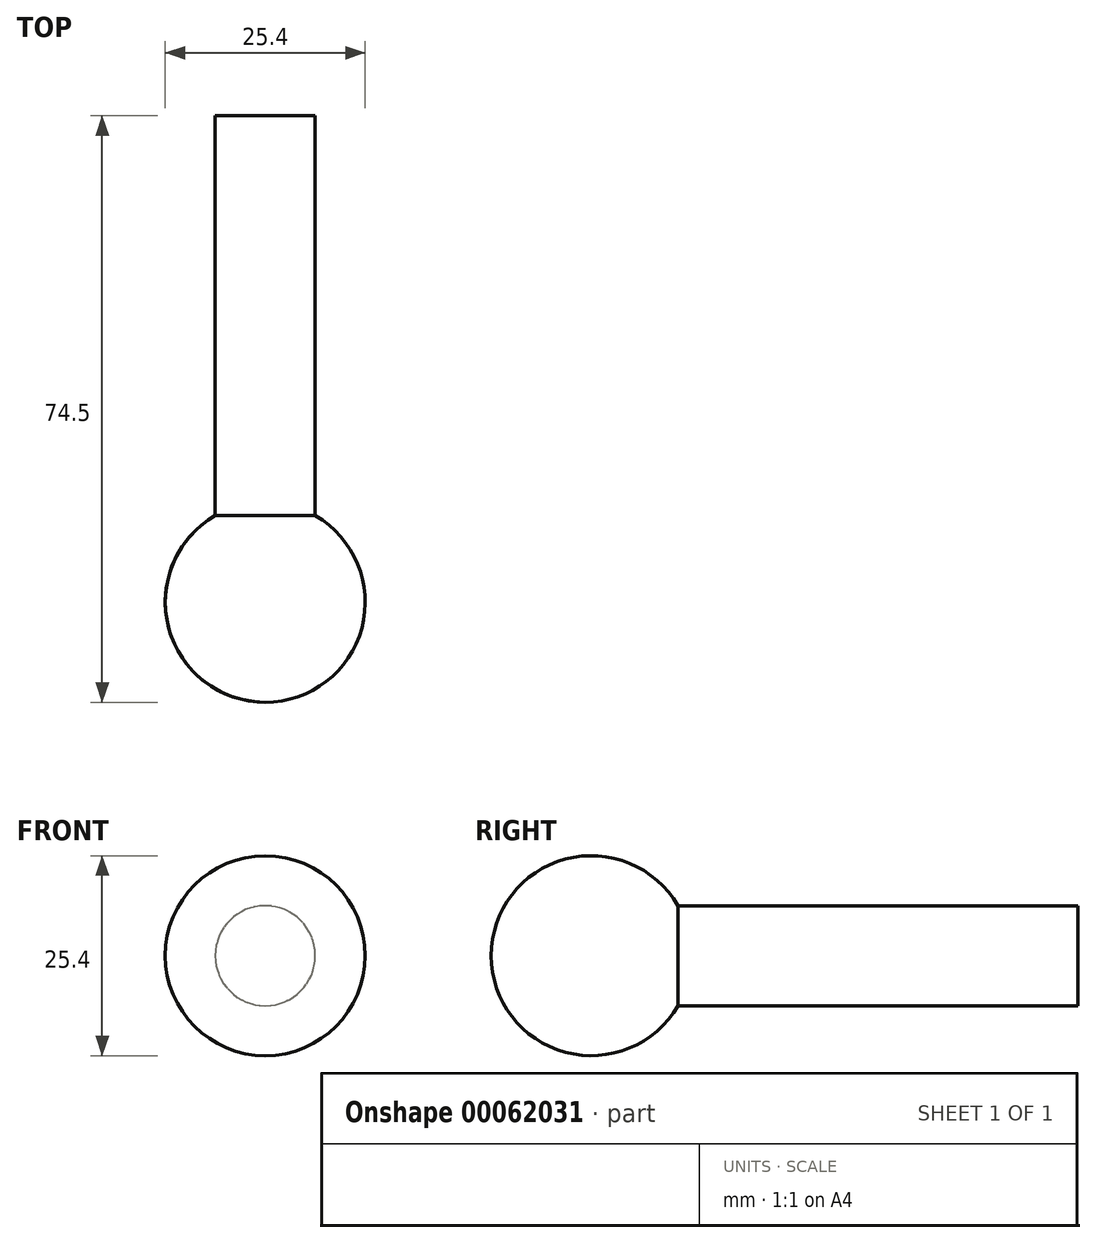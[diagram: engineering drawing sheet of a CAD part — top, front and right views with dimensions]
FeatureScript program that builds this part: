
annotation { "Feature Type Name" : "Feature", "Feature Type Description" : "" }
export const myFeature = defineFeature(function(context is Context, id is Id, definition is map)
    precondition{}
    {
        {
            var Q0;
            Q0=qCreatedBy(makeId("Top.planeOp"),FACE);
            var sketch = newSketch(context, id + "F0", { "sketchPlane" : qUnion([Q0])});
            skLineSegment(sketch, "E0.rect.bottom", {"start": v(-6.35, 25.4) * mm, "end": v(6.35, 25.4) * mm});
            skLineSegment(sketch, "E0.rect.top", {"start": v(-6.35, -25.4) * mm, "end": v(6.35, -25.4) * mm});
            skLineSegment(sketch, "E0.rect.left", {"start": v(-6.35, 25.4) * mm, "end": v(-6.35, -25.4) * mm});
            skLineSegment(sketch, "E0.rect.right", {"start": v(6.35, 25.4) * mm, "end": v(6.35, -25.4) * mm});
            skPoint(sketch, "E0.rect.middle", {"position": v(0, 0) * mm});
            skCircle(sketch, "E1", {"center": v(0, 36.4) * mm, "radius": 12.7 * mm});
            skPoint(sketch, "E2", {"position": v(0, 25.4) * mm});
            skCircle(sketch, "E3.MirrorC", {"center": v(0, -36.4) * mm, "radius": 12.7 * mm});
            skLineSegment(sketch, "E4", {"start": v(0, 49.1) * mm, "end": v(0, -49.1) * mm});
            skSolve(sketch);
        }
        {
            var Q0;
            {var subQ0=sQuery(id+"F0.wireOp",EDGE,"E1");var subQ3=sQuery(id+"F0.wireOp",EDGE,"E4");var subQ5=makeQuery(id+"F0.imprint","INTERSECT",VERTEX,{"disambiguationData":[OD(0.0)],"derivedFrom":[subQ0,subQ3]});Q0=makeQuery(id+"F0.imprint","IMPRINT",FACE,{"disambiguationData":[TD([[makeQuery(id+"F0.imprint","IMPRINT",EDGE,{"disambiguationData":[TD([[subQ5,-1.0]])],"derivedFrom":subQ3}),-1.0]])]});}
            var Q1;
            {var subQ1=sQuery(id+"F0.wireOp",EDGE,"E0.rect.bottom");var subQ3=sQuery(id+"F0.wireOp",EDGE,"E4");var subQ4=makeQuery(id+"F0.imprint","INTERSECT",VERTEX,{"derivedFrom":[subQ1,subQ3]});Q1=makeQuery(id+"F0.imprint","IMPRINT",FACE,{"disambiguationData":[TD([[makeQuery(id+"F0.imprint","IMPRINT",EDGE,{"disambiguationData":[TD([[subQ4,-1.0]])],"derivedFrom":subQ3}),-1.0]])]});}
            var Q2;
            {var subQ0=sQuery(id+"F0.wireOp",EDGE,"E0.rect.left");Q2=makeQuery(id+"F0.imprint","IMPRINT",FACE,{"disambiguationData":[TD([[makeQuery(id+"F0.imprint","IMPRINT",EDGE,{"derivedFrom":subQ0}),1.0]])]});}
            var Q3;
            {var subQ1=sQuery(id+"F0.wireOp",EDGE,"E0.rect.top");var subQ3=sQuery(id+"F0.wireOp",EDGE,"E4");var subQ4=makeQuery(id+"F0.imprint","INTERSECT",VERTEX,{"derivedFrom":[subQ1,subQ3]});Q3=makeQuery(id+"F0.imprint","IMPRINT",FACE,{"disambiguationData":[TD([[makeQuery(id+"F0.imprint","IMPRINT",EDGE,{"disambiguationData":[TD([[subQ4,1.0]])],"derivedFrom":subQ3}),-1.0]])]});}
            var Q4;
            {var subQ0=sQuery(id+"F0.wireOp",EDGE,"E3.MirrorC");var subQ3=sQuery(id+"F0.wireOp",EDGE,"E4");var subQ5=makeQuery(id+"F0.imprint","INTERSECT",VERTEX,{"disambiguationData":[OD(0.0)],"derivedFrom":[subQ0,subQ3]});Q4=makeQuery(id+"F0.imprint","IMPRINT",FACE,{"disambiguationData":[TD([[makeQuery(id+"F0.imprint","IMPRINT",EDGE,{"disambiguationData":[TD([[subQ5,1.0]])],"derivedFrom":subQ3}),-1.0]])]});}
            var Q5;
            Q5=sQuery(id+"F0.wireOp",EDGE,"E4");
            revolve(context, id + "F1", {"entities" : qUnion([Q0, Q1, Q2, Q3, Q4]), "axis" : qUnion([Q5]), "revolveType" : RevolveType.FULL});
        }
    });
